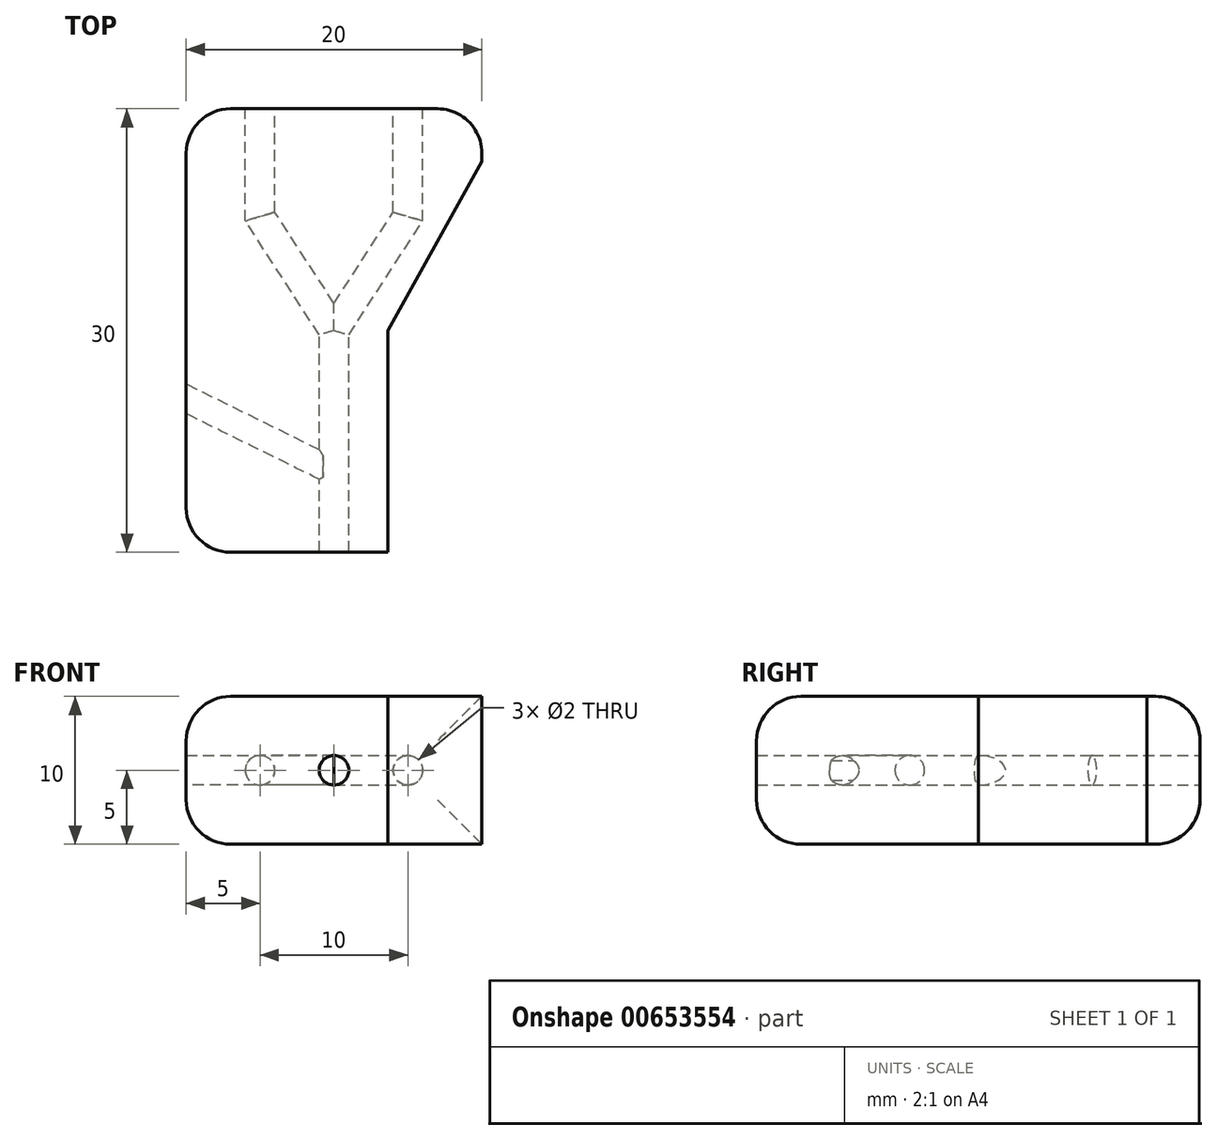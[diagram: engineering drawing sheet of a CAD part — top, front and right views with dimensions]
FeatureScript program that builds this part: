
annotation { "Feature Type Name" : "Feature", "Feature Type Description" : "" }
export const myFeature = defineFeature(function(context is Context, id is Id, definition is map)
    precondition{}
    {
        {
            var Q0;
            Q0=qCreatedBy(makeId("Top.planeOp"),FACE);
            var sketch = newSketch(context, id + "F0", { "sketchPlane" : qUnion([Q0])});
            skLineSegment(sketch, "E0.bottom", {"start": v(0, 15) * mm, "end": v(10, 15) * mm});
            skLineSegment(sketch, "E0.top", {"start": v(0, -15) * mm, "end": v(10, -15) * mm});
            skLineSegment(sketch, "E0.left", {"start": v(0, 15) * mm, "end": v(0, -15) * mm});
            skLineSegment(sketch, "E0.right", {"start": v(10, 15) * mm, "end": v(10, -15) * mm});
            skSolve(sketch);
        }
        {
            var Q0;
            Q0 = qSketchRegion(id + "F0", true);
            extrude(context, id + "F1", {"entities" : qUnion([Q0]), "depth" : 5 * mm, "offsetDistance" : 25 * mm});
        }
        {
            var Q0;
            Q0=makeQuery(id+"F1.opExtrude","CAP_FACE",FACE,{"disambiguationData":[OSD([sQuery(id+"F0.wireOp",EDGE,"E0.bottom"),sQuery(id+"F0.wireOp",EDGE,"E0.top"),sQuery(id+"F0.wireOp",EDGE,"E0.left"),sQuery(id+"F0.wireOp",EDGE,"E0.right")])],"isStart":false});
            var sketch = newSketch(context, id + "F2", { "sketchPlane" : qUnion([Q0])});
            skLineSegment(sketch, "E1", {"start": v(5, 15) * mm, "end": v(5, 7.7) * mm});
            skLineSegment(sketch, "E2", {"start": v(5, 7.7) * mm, "end": v(0, 0) * mm});
            skLineSegment(sketch, "E3", {"start": v(0, 0) * mm, "end": v(0, -15) * mm});
            skLineSegment(sketch, "E4.MirrorCS", {"start": v(-5, 15) * mm, "end": v(-5, 7.7) * mm, "construction": true});
            skLineSegment(sketch, "E5.MirrorCS", {"start": v(-5, 7.7) * mm, "end": v(0, 0) * mm, "construction": true});
            skSolve(sketch);
        }
        {
            var Q0;
            Q0=makeQuery(id+"F1.opExtrude","SWEPT_FACE",FACE,{"disambiguationData":[OSD([sQuery(id+"F0.wireOp",EDGE,"E0.top")])]});
            var sketch = newSketch(context, id + "F3", { "sketchPlane" : qUnion([Q0])});
            skCircle(sketch, "E6", {"center": v(0, 5) * mm, "radius": 1 * mm});
            skSolve(sketch);
        }
        {
            var Q0;
            Q0 = qSketchRegion(id + "F3", true);
            var Q1;
            Q1 = qConstructionFilter(qBodyType(qCreatedBy(id + "F2" ,EDGE), BodyType.WIRE), ConstructionObject.NO);
            sweep(context, id + "F4", {"operationType" : NewBodyOperationType.REMOVE, "profiles" : qUnion([Q0]), "path" : qUnion([Q1])});
        }
        {
            var Q0;
            Q0=makeQuery(id+"F1.opExtrude","SWEPT_BODY",BODY,{"disambiguationData":[OSD([sQuery(id+"F0.wireOp",EDGE,"E0.bottom"),sQuery(id+"F0.wireOp",EDGE,"E0.top"),sQuery(id+"F0.wireOp",EDGE,"E0.left"),sQuery(id+"F0.wireOp",EDGE,"E0.right")])]});
            var Q1;
            Q1=makeQuery(id+"F1.opExtrude","SWEPT_FACE",FACE,{"disambiguationData":[OSD([sQuery(id+"F0.wireOp",EDGE,"E0.left")])]});
            mirror(context, id + "F5", {"operationType" : NewBodyOperationType.ADD, "entities" : qUnion([Q0]), "mirrorPlane" : qUnion([Q1])});
        }
        {
            var Q0;
            {var subQ1=sQuery(id+"F0.wireOp",EDGE,"E0.bottom");var subQ2=sQuery(id+"F0.wireOp",EDGE,"E0.top");var subQ3=sQuery(id+"F0.wireOp",EDGE,"E0.right");Q0=makeQuery(id+"F4.boolean.opBoolean","SPLIT",FACE,{"disambiguationData":[TD([makeQuery(id+"F1.opExtrude","SWEPT_FACE",FACE,{"disambiguationData":[OSD([subQ2])]})])],"derivedFrom":makeQuery(id+"F1.opExtrude","CAP_FACE",FACE,{"disambiguationData":[OSD([subQ1,subQ2,sQuery(id+"F0.wireOp",EDGE,"E0.left"),subQ3])],"isStart":false})});}
            var sketch = newSketch(context, id + "F6", { "sketchPlane" : qUnion([Q0])});
            skLineSegment(sketch, "E7", {"start": v(-0.75, -9.25) * mm, "end": v(-10.17, -4.6) * mm});
            skLineSegment(sketch, "E8.0", {"start": v(6, 7.4) * mm, "end": v(6, 15) * mm, "construction": true});
            skLineSegment(sketch, "E9.0", {"start": v(1, -0.3) * mm, "end": v(6, 7.4) * mm, "construction": true});
            skLineSegment(sketch, "E10.0", {"start": v(-1, -0.3) * mm, "end": v(-6, 7.4) * mm, "construction": true});
            skLineSegment(sketch, "E11.0", {"start": v(-6, 7.4) * mm, "end": v(-6, 15) * mm, "construction": true});
            skLineSegment(sketch, "E12.0", {"start": v(1, -15) * mm, "end": v(1, -0.3) * mm, "construction": true});
            skLineSegment(sketch, "E13.0", {"start": v(-4, 15) * mm, "end": v(-4, 8) * mm, "construction": true});
            skSolve(sketch);
        }
        {
            var Q0;
            Q0=makeQuery(id+"F5.opPattern","COPY",FACE,{"derivedFrom":makeQuery(id+"F1.opExtrude","SWEPT_FACE",FACE,{"disambiguationData":[OSD([sQuery(id+"F0.wireOp",EDGE,"E0.right")])]}),"instanceName":"1"});
            var sketch = newSketch(context, id + "F7", { "sketchPlane" : qUnion([Q0])});
            skCircle(sketch, "E14", {"center": v(4.64, 5) * mm, "radius": 1 * mm});
            skSolve(sketch);
        }
        {
            var Q0;
            {var subQ0=sQuery(id+"F7.wireOp",EDGE,"E14");var subQ1=makeQuery(id+"F5.opPattern","COPY",EDGE,{"derivedFrom":makeQuery(id+"F1.opExtrude","CAP_EDGE",EDGE,{"disambiguationData":[OSD([sQuery(id+"F0.wireOp",EDGE,"E0.right")])],"isStart":false}),"instanceName":"1"});var subQ2=makeQuery(id+"F7.imprint","INTERSECT",VERTEX,{"disambiguationData":[OD(0.0)],"derivedFrom":[subQ1,subQ0]});Q0=makeQuery(id+"F7.imprint","IMPRINT",FACE,{"disambiguationData":[TD([[makeQuery(id+"F7.imprint","IMPRINT",EDGE,{"disambiguationData":[TD([[subQ2,1.0]])],"derivedFrom":subQ0}),1.0]])]});}
            var Q1;
            {var subQ0=sQuery(id+"F7.wireOp",EDGE,"E14");var subQ1=makeQuery(id+"F5.opPattern","COPY",EDGE,{"derivedFrom":makeQuery(id+"F1.opExtrude","CAP_EDGE",EDGE,{"disambiguationData":[OSD([sQuery(id+"F0.wireOp",EDGE,"E0.right")])],"isStart":false}),"instanceName":"1"});var subQ2=makeQuery(id+"F7.imprint","INTERSECT",VERTEX,{"disambiguationData":[OD(0.0)],"derivedFrom":[subQ1,subQ0]});Q1=makeQuery(id+"F7.imprint","IMPRINT",FACE,{"disambiguationData":[TD([[makeQuery(id+"F7.imprint","IMPRINT",EDGE,{"disambiguationData":[TD([[subQ2,-1.0]])],"derivedFrom":subQ0}),1.0]])]});}
            var Q2;
            Q2=sQuery(id+"F6.wireOp",EDGE,"E7");
            sweep(context, id + "F8", {"operationType" : NewBodyOperationType.REMOVE, "profiles" : qUnion([Q0, Q1]), "path" : qUnion([Q2])});
        }
        {
            var Q0;
            Q0=makeQuery(id+"F1.opExtrude","SWEPT_BODY",BODY,{"disambiguationData":[OSD([sQuery(id+"F0.wireOp",EDGE,"E0.bottom"),sQuery(id+"F0.wireOp",EDGE,"E0.top"),sQuery(id+"F0.wireOp",EDGE,"E0.left"),sQuery(id+"F0.wireOp",EDGE,"E0.right")])]});
            var Q1;
            {var subQ2=sQuery(id+"F0.wireOp",EDGE,"E0.right");var subQ6=sQuery(id+"F0.wireOp",EDGE,"E0.bottom");var subQ7=makeQuery(id+"F1.opExtrude","SWEPT_FACE",FACE,{"disambiguationData":[OSD([subQ6])]});var subQ9=sQuery(id+"F0.wireOp",EDGE,"E0.top");Q1=makeQuery(id+"F8.boolean.opBoolean","SPLIT",FACE,{"disambiguationData":[TD([subQ7])],"derivedFrom":makeQuery(id+"F5.opPattern","COPY",FACE,{"derivedFrom":makeQuery(id+"F4.boolean.opBoolean","SPLIT",FACE,{"disambiguationData":[TD([makeQuery(id+"F1.opExtrude","SWEPT_FACE",FACE,{"disambiguationData":[OSD([subQ9])]})])],"derivedFrom":makeQuery(id+"F1.opExtrude","CAP_FACE",FACE,{"disambiguationData":[OSD([subQ6,subQ9,sQuery(id+"F0.wireOp",EDGE,"E0.left"),subQ2])],"isStart":false})}),"instanceName":"1"})});}
            mirror(context, id + "F9", {"operationType" : NewBodyOperationType.ADD, "entities" : qUnion([Q0]), "mirrorPlane" : qUnion([Q1])});
        }
        {
            var Q0;
            {var subQ0=makeQuery(id+"F1.opExtrude","CAP_FACE",FACE,{"disambiguationData":[OSD([sQuery(id+"F0.wireOp",EDGE,"E0.bottom"),sQuery(id+"F0.wireOp",EDGE,"E0.top"),sQuery(id+"F0.wireOp",EDGE,"E0.left"),sQuery(id+"F0.wireOp",EDGE,"E0.right")])],"isStart":true});Q0=makeQuery(id+"F9.opPattern","COPY",FACE,{"derivedFrom":makeQuery(id+"F5.boolean.opBoolean","MERGE",FACE,{"derivedFrom":[subQ0,makeQuery(id+"F5.opPattern","COPY",FACE,{"derivedFrom":subQ0,"instanceName":"1"})]}),"instanceName":"1"});}
            var sketch = newSketch(context, id + "F10", { "sketchPlane" : qUnion([Q0])});
            skLineSegment(sketch, "E15", {"start": v(10, 11.41) * mm, "end": v(3.66, 0) * mm});
            skLineSegment(sketch, "E16", {"start": v(3.66, 0) * mm, "end": v(3.66, -15) * mm});
            skLineSegment(sketch, "E17", {"start": v(3.66, -15) * mm, "end": v(10, -15) * mm});
            skLineSegment(sketch, "E18", {"start": v(10, -15) * mm, "end": v(10, 11.41) * mm});
            skSolve(sketch);
        }
        {
            var Q0;
            Q0 = qSketchRegion(id + "F10", true);
            extrude(context, id + "F11", {"entities" : qUnion([Q0]), "operationType" : NewBodyOperationType.REMOVE, "oppositeDirection" : true, "depth" : 10 * mm, "offsetDistance" : 25 * mm});
        }
        {
            var Q0;
            Q0=makeQuery(id+"F11.boolean.opBoolean","COPY",EDGE,{"derivedFrom":makeQuery(id+"F11.opExtrude","CAP_EDGE",EDGE,{"disambiguationData":[OSD([sQuery(id+"F10.wireOp",EDGE,"E16")])],"isStart":true})});
            var Q1;
            Q1=makeQuery(id+"F11.boolean.opBoolean","COPY",EDGE,{"derivedFrom":makeQuery(id+"F11.opExtrude","CAP_EDGE",EDGE,{"disambiguationData":[OSD([sQuery(id+"F10.wireOp",EDGE,"E16")])],"isStart":false})});
            var Q2;
            {var subQ0=makeQuery(id+"F1.opExtrude","CAP_EDGE",EDGE,{"disambiguationData":[OSD([sQuery(id+"F0.wireOp",EDGE,"E0.top")])],"isStart":true});Q2=makeQuery(id+"F9.opPattern","COPY",EDGE,{"derivedFrom":makeQuery(id+"F5.boolean.opBoolean","MERGE",EDGE,{"derivedFrom":[subQ0,makeQuery(id+"F5.opPattern","COPY",EDGE,{"derivedFrom":subQ0,"instanceName":"1"})]}),"instanceName":"1"});}
            var Q3;
            Q3=makeQuery(id+"F11.boolean.opBoolean","COPY",EDGE,{"derivedFrom":makeQuery(id+"F11.opExtrude","SWEPT_EDGE",EDGE,{"disambiguationData":[OSD([sQuery(id+"F0.wireOp",EDGE,"E0.top"),sQuery(id+"F10.wireOp",EDGE,"E16"),sQuery(id+"F10.wireOp",EDGE,"E17")])]})});
            var Q4;
            {var subQ0=makeQuery(id+"F5.opPattern","COPY",EDGE,{"derivedFrom":makeQuery(id+"F1.opExtrude","SWEPT_EDGE",EDGE,{"disambiguationData":[OSD([sQuery(id+"F0.wireOp",EDGE,"E0.top"),sQuery(id+"F0.wireOp",EDGE,"E0.right")])]}),"instanceName":"1"});Q4=makeQuery(id+"F9.boolean.opBoolean","MERGE",EDGE,{"derivedFrom":[subQ0,makeQuery(id+"F9.opPattern","COPY",EDGE,{"derivedFrom":subQ0,"instanceName":"1"})]});}
            var Q5;
            {var subQ0=makeQuery(id+"F1.opExtrude","CAP_EDGE",EDGE,{"disambiguationData":[OSD([sQuery(id+"F0.wireOp",EDGE,"E0.top")])],"isStart":true});Q5=makeQuery(id+"F5.boolean.opBoolean","MERGE",EDGE,{"derivedFrom":[subQ0,makeQuery(id+"F5.opPattern","COPY",EDGE,{"derivedFrom":subQ0,"instanceName":"1"})]});}
            var Q6;
            Q6=makeQuery(id+"F5.opPattern","COPY",EDGE,{"derivedFrom":makeQuery(id+"F1.opExtrude","CAP_EDGE",EDGE,{"disambiguationData":[OSD([sQuery(id+"F0.wireOp",EDGE,"E0.right")])],"isStart":true}),"instanceName":"1"});
            var Q7;
            Q7=makeQuery(id+"F9.opPattern","COPY",EDGE,{"derivedFrom":makeQuery(id+"F5.opPattern","COPY",EDGE,{"derivedFrom":makeQuery(id+"F1.opExtrude","CAP_EDGE",EDGE,{"disambiguationData":[OSD([sQuery(id+"F0.wireOp",EDGE,"E0.right")])],"isStart":true}),"instanceName":"1"}),"instanceName":"1"});
            var Q8;
            Q8=makeQuery(id+"F11.boolean.opBoolean","COPY",EDGE,{"derivedFrom":makeQuery(id+"F11.opExtrude","CAP_EDGE",EDGE,{"disambiguationData":[OSD([sQuery(id+"F10.wireOp",EDGE,"E15")])],"isStart":true})});
            var Q9;
            Q9=makeQuery(id+"F11.boolean.opBoolean","COPY",EDGE,{"derivedFrom":makeQuery(id+"F11.opExtrude","CAP_EDGE",EDGE,{"disambiguationData":[OSD([sQuery(id+"F10.wireOp",EDGE,"E15")])],"isStart":false})});
            var Q10;
            Q10=makeQuery(id+"F11.boolean.opBoolean","COPY",EDGE,{"derivedFrom":makeQuery(id+"F11.opExtrude","SWEPT_EDGE",EDGE,{"disambiguationData":[OSD([sQuery(id+"F0.wireOp",EDGE,"E0.right"),sQuery(id+"F10.wireOp",EDGE,"E15"),sQuery(id+"F10.wireOp",EDGE,"E18")])]})});
            var Q11;
            {var subQ0=makeQuery(id+"F1.opExtrude","CAP_EDGE",EDGE,{"disambiguationData":[OSD([sQuery(id+"F0.wireOp",EDGE,"E0.bottom")])],"isStart":true});Q11=makeQuery(id+"F5.boolean.opBoolean","MERGE",EDGE,{"derivedFrom":[subQ0,makeQuery(id+"F5.opPattern","COPY",EDGE,{"derivedFrom":subQ0,"instanceName":"1"})]});}
            var Q12;
            {var subQ0=makeQuery(id+"F1.opExtrude","CAP_EDGE",EDGE,{"disambiguationData":[OSD([sQuery(id+"F0.wireOp",EDGE,"E0.bottom")])],"isStart":true});Q12=makeQuery(id+"F9.opPattern","COPY",EDGE,{"derivedFrom":makeQuery(id+"F5.boolean.opBoolean","MERGE",EDGE,{"derivedFrom":[subQ0,makeQuery(id+"F5.opPattern","COPY",EDGE,{"derivedFrom":subQ0,"instanceName":"1"})]}),"instanceName":"1"});}
            var Q13;
            {var subQ0=makeQuery(id+"F1.opExtrude","SWEPT_EDGE",EDGE,{"disambiguationData":[OSD([sQuery(id+"F0.wireOp",EDGE,"E0.bottom"),sQuery(id+"F0.wireOp",EDGE,"E0.right")])]});Q13=makeQuery(id+"F9.boolean.opBoolean","MERGE",EDGE,{"derivedFrom":[subQ0,makeQuery(id+"F9.opPattern","COPY",EDGE,{"derivedFrom":subQ0,"instanceName":"1"})]});}
            var Q14;
            {var subQ0=makeQuery(id+"F5.opPattern","COPY",EDGE,{"derivedFrom":makeQuery(id+"F1.opExtrude","SWEPT_EDGE",EDGE,{"disambiguationData":[OSD([sQuery(id+"F0.wireOp",EDGE,"E0.bottom"),sQuery(id+"F0.wireOp",EDGE,"E0.right")])]}),"instanceName":"1"});Q14=makeQuery(id+"F9.boolean.opBoolean","MERGE",EDGE,{"derivedFrom":[subQ0,makeQuery(id+"F9.opPattern","COPY",EDGE,{"derivedFrom":subQ0,"instanceName":"1"})]});}
            fillet(context, id + "F12", {"entities" : qUnion([Q0, Q1, Q2, Q3, Q4, Q5, Q6, Q7, Q8, Q9, Q10, Q11, Q12, Q13, Q14]), "radius" : 3 * mm, "tangentPropagation" : true, "allowEdgeOverflow" : false});
        }
    });
